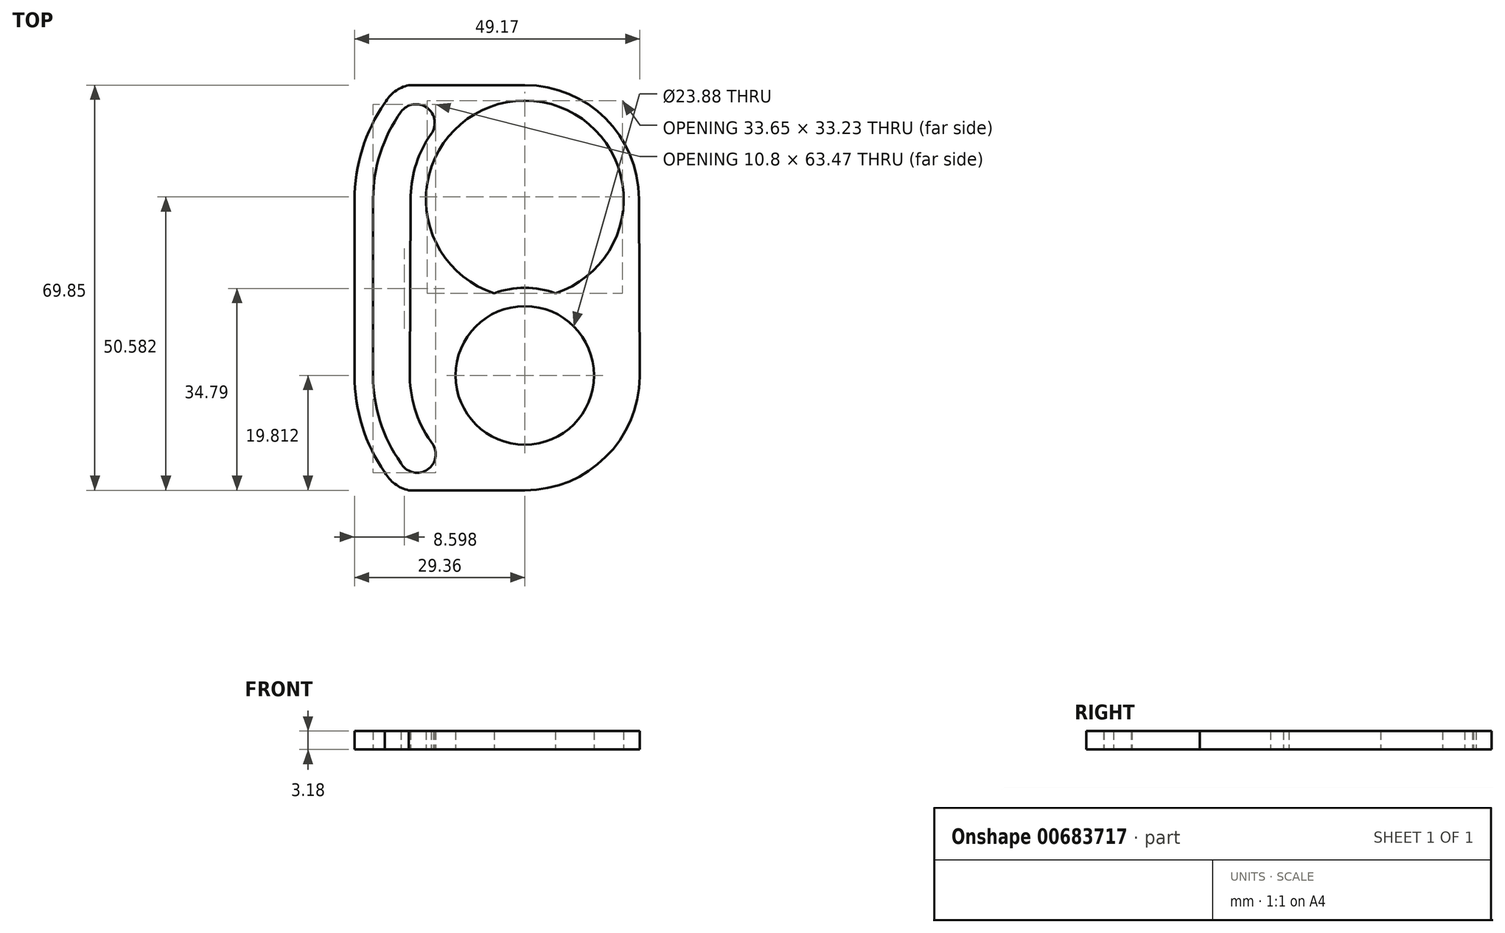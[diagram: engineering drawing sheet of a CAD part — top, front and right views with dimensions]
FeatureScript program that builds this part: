
annotation { "Feature Type Name" : "Feature", "Feature Type Description" : "" }
export const myFeature = defineFeature(function(context is Context, id is Id, definition is map)
    precondition{}
    {
        {
            var Q0;
            Q0=qCreatedBy(makeId("Top.planeOp"),FACE);
            var sketch = newSketch(context, id + "F0", { "sketchPlane" : qUnion([Q0])});
            skLineSegment(sketch, "E0.right", {"start": v(0, -19.69) * mm, "end": v(0, -19.69) * mm});
            skPoint(sketch, "E0.middle", {"position": v(0, 0) * mm});
            skLineSegment(sketch, "E1", {"start": v(0, 0) * mm, "end": v(0, -0.12) * mm});
            skArc(sketch, "E2", {"start": v(-13.03, 14.76) * mm, "mid": v(-17.82, 8.37) * mm, "end": v(-19.68, 0.6) * mm, "construction": true});
            skPoint(sketch, "E2.first.point", {"position": v(-19.68, 0.6) * mm});
            skPoint(sketch, "E2.third.point", {"position": v(19.69, 0.08) * mm});
            skArc(sketch, "E3", {"start": v(15.31, 7.47) * mm, "mid": v(0, 17.04) * mm, "end": v(-15.31, 7.47) * mm});
            skArc(sketch, "E4.cCircle", {"start": v(-19.81, -30.55) * mm, "mid": v(-18.73, -36.8) * mm, "end": v(-15.73, -42.39) * mm});
            skPoint(sketch, "E4.0.midPoint", {"position": v(7.4, -48.73) * mm});
            skPoint(sketch, "E5", {"position": v(19.81, -30.55) * mm});
            skPoint(sketch, "E6", {"position": v(-19.81, -30.55) * mm});
            skLineSegment(sketch, "E7", {"start": v(19.69, 0.08) * mm, "end": v(19.81, -30.55) * mm, "construction": true});
            skCircle(sketch, "E8", {"center": v(0, -30.35) * mm, "radius": 11.94 * mm});
            skLineSegment(sketch, "E9.right", {"start": v(-29.37, -0.5) * mm, "end": v(-29.37, -24.12) * mm});
            skPoint(sketch, "E10.start.orphan", {"position": v(19.81, -30.35) * mm});
            skLineSegment(sketch, "E11", {"start": v(19.81, -30.35) * mm, "end": v(-19.81, -30.55) * mm, "construction": true});
            skPoint(sketch, "E12", {"position": v(19.75, -15.24) * mm});
            skLineSegment(sketch, "E13.3", {"start": v(-29.37, -0.5) * mm, "end": v(-29.37, -0.5) * mm});
            skLineSegment(sketch, "E14.0", {"start": v(-29.37, -24.12) * mm, "end": v(-29.37, -20.95) * mm});
            skPoint(sketch, "E15", {"position": v(-29.37, -0.5) * mm});
            skArc(sketch, "E16.trimOffspring", {"start": v(-29.36, 0.57) * mm, "mid": v(-29.4, 0.04) * mm, "end": v(-29.37, -0.5) * mm});
            skLineSegment(sketch, "E17.0.right", {"start": v(-22.93, -6.4) * mm, "end": v(-22.93, -6.43) * mm});
            skLineSegment(sketch, "E18", {"start": v(-13.03, 14.76) * mm, "end": v(-13.03, 14.76) * mm});
            skLineSegment(sketch, "E19.trimOffspring", {"start": v(-22.93, -6.4) * mm, "end": v(-22.93, -6.43) * mm, "construction": true});
            skLineSegment(sketch, "E20.trimOffspring", {"start": v(-23.5, -30.85) * mm, "end": v(-23.5, -30.98) * mm, "construction": true});
            skLineSegment(sketch, "E21.bottom", {"start": v(0, 19.69) * mm, "end": v(-20, 19.69) * mm});
            skLineSegment(sketch, "E21.top", {"start": v(0, -50.16) * mm, "end": v(-20, -50.16) * mm});
            skLineSegment(sketch, "E21.right", {"start": v(-29.36, 0.57) * mm, "end": v(-29.36, -30.35) * mm});
            skLineSegment(sketch, "E22.1", {"start": v(-26.14, 13.62) * mm, "end": v(-26.14, 13.38) * mm});
            skLineSegment(sketch, "E23.MirrorCS", {"start": v(-19.68, 0.6) * mm, "end": v(-19.81, -30.55) * mm});
            skPoint(sketch, "E24", {"position": v(-19.68, 19.69) * mm});
            skArc(sketch, "E25.trimOffspring", {"start": v(19.69, 0.08) * mm, "mid": v(8.06, 17.96) * mm, "end": v(-13.03, 14.76) * mm, "construction": true});
            skLineSegment(sketch, "E26.trimOffspring", {"start": v(0, -30.35) * mm, "end": v(0, -30.45) * mm, "construction": true});
            skPoint(sketch, "E27", {"position": v(0, 19.69) * mm});
            skArc(sketch, "E28", {"start": v(19.69, 0.08) * mm, "mid": v(13.9, 13.95) * mm, "end": v(0, 19.69) * mm});
            skArc(sketch, "E29", {"start": v(-26.14, -0.02) * mm, "mid": v(-24.92, 7.9) * mm, "end": v(-21.35, 15.09) * mm});
            skArc(sketch, "E30", {"start": v(-26.16, -30.35) * mm, "mid": v(-24.93, -38.27) * mm, "end": v(-21.36, -45.45) * mm});
            skArc(sketch, "E31", {"start": v(-15.73, -42.39) * mm, "mid": v(-15.42, -44.62) * mm, "end": v(-16.65, -46.5) * mm});
            skArc(sketch, "E32", {"start": v(-16.15, 11.26) * mm, "mid": v(-15.57, 13.73) * mm, "end": v(-16.96, 15.86) * mm});
            skPoint(sketch, "E32.first.point", {"position": v(-16.15, 11.26) * mm});
            skPoint(sketch, "E32.third.point", {"position": v(-16.15, 11.26) * mm});
            skArc(sketch, "E33", {"start": v(-29.36, -30.35) * mm, "mid": v(-28.02, -39.1) * mm, "end": v(-24.13, -47.07) * mm});
            skArc(sketch, "E34", {"start": v(-29.36, 0.57) * mm, "mid": v(-28.48, 7.16) * mm, "end": v(-26.14, 13.38) * mm});
            skPoint(sketch, "E35.orphan", {"position": v(-22.86, 16.51) * mm});
            skLineSegment(sketch, "E36.trimOffspring", {"start": v(-26.14, 0.13) * mm, "end": v(-26.16, -30.35) * mm});
            skPoint(sketch, "E37.orphan", {"position": v(-19.63, 13.6) * mm});
            skLineSegment(sketch, "E38.trimOffspring", {"start": v(-26.17, -43.65) * mm, "end": v(-26.17, -43.72) * mm});
            skArc(sketch, "E39", {"start": v(-19.68, 0.6) * mm, "mid": v(-18.7, 6.19) * mm, "end": v(-16.15, 11.26) * mm});
            skLineSegment(sketch, "E40", {"start": v(19.69, 0.08) * mm, "end": v(19.81, -30.55) * mm});
            skArc(sketch, "E41", {"start": v(0, -50.16) * mm, "mid": v(14, -44.36) * mm, "end": v(19.81, -30.35) * mm});
            skArc(sketch, "E42", {"start": v(-15.73, -42.39) * mm, "mid": v(-8.77, -48.11) * mm, "end": v(0, -50.16) * mm, "construction": true});
            skLineSegment(sketch, "E43", {"start": v(-24.13, -47.07) * mm, "end": v(-24.13, -47.07) * mm});
            skArc(sketch, "E44", {"start": v(-24.13, -47.07) * mm, "mid": v(-22.4, -49.05) * mm, "end": v(-20, -50.16) * mm});
            skArc(sketch, "E45", {"start": v(-16.65, -46.5) * mm, "mid": v(-19.24, -47.05) * mm, "end": v(-21.36, -45.45) * mm});
            skLineSegment(sketch, "E46", {"start": v(-21.35, 15.09) * mm, "end": v(-21.35, 15.09) * mm});
            skArc(sketch, "E47", {"start": v(-16.96, 15.86) * mm, "mid": v(-19.3, 16.35) * mm, "end": v(-21.35, 15.09) * mm});
            skArc(sketch, "E48", {"start": v(5.3, -16.2) * mm, "mid": v(0, 17.04) * mm, "end": v(-5.3, -16.2) * mm});
            skArc(sketch, "E49", {"start": v(-5.3, -16.2) * mm, "mid": v(0, -45.46) * mm, "end": v(5.3, -16.2) * mm, "construction": true});
            skArc(sketch, "E50", {"start": v(5.3, -16.2) * mm, "mid": v(0, -15.24) * mm, "end": v(-5.3, -16.2) * mm});
            skPoint(sketch, "E51.center.orphan", {"position": v(0, 1.4) * mm});
            skPoint(sketch, "E52", {"position": v(0, -15.24) * mm});
            skArc(sketch, "E53.MirrorCS", {"start": v(-24.13, 16.6) * mm, "mid": v(-22.4, 18.58) * mm, "end": v(-20, 19.69) * mm});
            skArc(sketch, "E54.MirrorCS", {"start": v(-29.36, -0.12) * mm, "mid": v(-28.02, 8.64) * mm, "end": v(-24.13, 16.6) * mm});
            skLineSegment(sketch, "E55.trimOffspring", {"start": v(0, -30.35) * mm, "end": v(0, -30.45) * mm});
            skSolve(sketch);
        }
        {
            var Q0;
            {var subQ5=sQuery(id+"F0.wireOp",EDGE,"E21.bottom");Q0=makeQuery(id+"F0.imprint","IMPRINT",FACE,{"disambiguationData":[TD([[makeQuery(id+"F0.imprint","IMPRINT",EDGE,{"derivedFrom":subQ5}),1.0]])]});}
            var Q1;
            {var subQ9=sQuery(id+"F0.wireOp",EDGE,"qnDXpv8G-ciFG-gFAo-xOLX-AdnHt3FC98V8");Q1=makeQuery(id+"F0.imprint","IMPRINT",FACE,{"disambiguationData":[TD([[makeQuery(id+"F0.imprint","IMPRINT",EDGE,{"derivedFrom":subQ9}),-1.0]])]});}
            var Q2;
            Q2 = qSketchRegion(id + "FI1SJGL3qkMEE7U_1", true);
            extrude(context, id + "F1", {"entities" : qUnion([Q0, Q1, Q2]), "depth" : 3.17 * mm, "offsetDistance" : 25.4 * mm});
        }
    });
